FCSTD DOCUMENT  (FreeCAD 0.19R24267 +148 (Git))
Label: Idle Plate
License: All rights reserved
LicenseURL: http://en.wikipedia.org/wiki/All_rights_reserved
objects: Sketcher::SketchObject×2, Part::Part2DObjectPython×1, PartDesign::Body×1
note: 4 computed .brp shape members not serialized (recipe doc carries the construction recipe); baked Part::Feature solids carry a one-line shape summary decoded from their .brp

FEATURE [Sketcher::SketchObject] Sketch
  FullyConstrained = false
  MapMode = 5
  Support = -> [XY_Plane]
  sketch-geometry (27):
    g0: Circle CenterX=0 CenterY=0 CenterZ=0 NormalX=0 NormalY=0 NormalZ=1 AngleXU=0 Radius=15
    g1: Circle CenterX=0 CenterY=0 CenterZ=0 NormalX=0 NormalY=0 NormalZ=1 AngleXU=0 Radius=25
    g2: Circle CenterX=-30 CenterY=71.7924 CenterZ=0 NormalX=0 NormalY=0 NormalZ=1 AngleXU=0 Radius=24
    g3: Circle CenterX=-30 CenterY=71.7924 CenterZ=0 NormalX=0 NormalY=0 NormalZ=1 AngleXU=0 Radius=12
    g4: ArcOfCircle CenterX=-110 CenterY=0 CenterZ=0 NormalX=0 NormalY=0 NormalZ=1 AngleXU=0 Radius=25 StartAngle=1.5708 EndAngle=4.71239
    g5: ArcOfCircle CenterX=-75 CenterY=1.2e-15 CenterZ=0 NormalX=0 NormalY=0 NormalZ=1 AngleXU=0 Radius=25 StartAngle=4.71239 EndAngle=7.85398
    g6: LineSegment StartX=-110 StartY=-25 StartZ=0 EndX=-75 EndY=-25 EndZ=0
    g7: LineSegment StartX=-110 StartY=25 StartZ=0 EndX=-75 EndY=25 EndZ=0
    g8: ArcOfCircle CenterX=-110 CenterY=0 CenterZ=0 NormalX=0 NormalY=0 NormalZ=1 AngleXU=0 Radius=13 StartAngle=1.5708 EndAngle=4.71239
    g9: ArcOfCircle CenterX=-76.4586 CenterY=0 CenterZ=0 NormalX=0 NormalY=0 NormalZ=1 AngleXU=0 Radius=13 StartAngle=4.71239 EndAngle=7.85398
    g10: LineSegment StartX=-110 StartY=-13 StartZ=0 EndX=-76.4586 EndY=-13 EndZ=0
    g11: LineSegment StartX=-110 StartY=13 StartZ=0 EndX=-76.4586 EndY=13 EndZ=0
    g12: ArcOfCircle CenterX=79.9751 CenterY=0.000354198 CenterZ=0 NormalX=0 NormalY=0 NormalZ=1 AngleXU=0 Radius=12 StartAngle=3.04319 EndAngle=6.18992
    g13: ArcOfCircle CenterX=42.853 CenterY=65.8804 CenterZ=0 NormalX=0 NormalY=0 NormalZ=1 AngleXU=0 Radius=12 StartAngle=1.11953 EndAngle=4.26626
    g14: ArcOfCircle CenterX=42.853 CenterY=65.8804 CenterZ=0 NormalX=0 NormalY=0 NormalZ=1 AngleXU=0 Radius=23.9932 StartAngle=1.11953 EndAngle=4.28028
    g15: ArcOfCircle CenterX=-105.35 CenterY=76.497 CenterZ=0 NormalX=0 NormalY=0 NormalZ=1 AngleXU=0 Radius=51.497 StartAngle=4.71239 EndAngle=6.22083
    g16: ArcOfCircle CenterX=7.39019 CenterY=80.6675 CenterZ=0 NormalX=0 NormalY=0 NormalZ=1 AngleXU=0 Radius=14.4291 StartAngle=3.37464 EndAngle=5.88813
    g17: ArcOfCircle CenterX=13.9205 CenterY=6.17871 CenterZ=0 NormalX=0 NormalY=0 NormalZ=1 AngleXU=0 Radius=90.3361 StartAngle=6.18992 EndAngle=7.40272
    g18: ArcOfCircle CenterX=15.8002 CenterY=7.21933 CenterZ=0 NormalX=0 NormalY=0 NormalZ=1 AngleXU=0 Radius=40.6054 StartAngle=6.17117 EndAngle=7.42188
    g19: LineSegment StartX=-110 StartY=-25 StartZ=0 EndX=-16.1843 EndY=-43.4398 EndZ=0
    g20: LineSegment StartX=17.5699 StartY=-34.5542 StartZ=0 EndX=35.6596 EndY=-19.0405 EndZ=0
    g21: LineSegment StartX=53.6215 StartY=-15.8217 StartZ=0 EndX=70.8829 EndY=-22.206 EndZ=0
    g22: ArcOfCircle CenterX=-8.46974 CenterY=-4.19076 CenterZ=0 NormalX=0 NormalY=0 NormalZ=1 AngleXU=0 Radius=40 StartAngle=4.51831 EndAngle=5.42128
    g23: ArcOfCircle CenterX=47.3774 CenterY=-32.704 CenterZ=0 NormalX=0 NormalY=0 NormalZ=1 AngleXU=0 Radius=18 StartAngle=1.21654 EndAngle=2.27969
    g24: ArcOfCircle CenterX=13.9205 CenterY=6.17872 CenterZ=0 NormalX=0 NormalY=0 NormalZ=1 AngleXU=0 Radius=78.3429 StartAngle=6.18992 EndAngle=7.40272
    g25: ArcOfCircle CenterX=14.438 CenterY=6.47035 CenterZ=0 NormalX=0 NormalY=0 NormalZ=1 AngleXU=0 Radius=53.8556 StartAngle=6.18478 EndAngle=7.40786
    g26: ArcOfCircle CenterX=79.9845 CenterY=-0.000734032 CenterZ=0 NormalX=0 NormalY=0 NormalZ=1 AngleXU=0 Radius=23.9837 StartAngle=3.02957 EndAngle=6.18992
  constraints (52):
    c: Coincident(g0,g-1)
    c: Coincident(g1,g0)
    c: Coincident(g3,g2)
    c: Diameter(g3) = 24
    c: DistanceX(g2,g0) = 30
    c: Tangent(g4,g7) = 1.5708
    c: Tangent(g4,g6) = -1.5708
    c: Tangent(g6,g5) = -1.5708
    c: Tangent(g7,g5) = 1.5708
    c: Horizontal(g6)
    c: Equal(g4,g5)
    c: PointOnObject(g4,g-1)
    c: Tangent(g8,g11) = 1.5708
    c: Tangent(g8,g10) = -1.5708
    c: Tangent(g10,g9) = -1.5708
    c: Tangent(g11,g9) = 1.5708
    c: Horizontal(g10)
    c: Equal(g8,g9)
    c: Coincident(g8,g4)
    c: DistanceX(g4,g5) = 35
    c: Radius(g4) = 25
    c: Radius(g1) = 25
    c: Radius(g8) = 13
    c: Radius(g0) = 15
    c: Radius(g12) = 12
    c: Coincident(g13,g14)
    c: Equal(g12,g13) = 13
    c: PointOnObject(g15,g7)
    c: PointOnObject(g15,g2)
    c: Tangent(g2,g15)
    c: Tangent(g7,g15)
    c: PointOnObject(g16,g2)
    c: PointOnObject(g16,g14)
    c: Tangent(g2,g16)
    c: Tangent(g16,g14)
    c: Coincident(g19,g4)
    c: Tangent(g19,g22) = -1.5708
    c: Tangent(g20,g22) = -1.5708
    c: Tangent(g21,g23) = 1.5708
    c: Tangent(g20,g23) = 1.5708
    c: Tangent(g13,g24) = -1.5708
    c: Tangent(g13,g25) = 1.5708
    c: Tangent(g14,g18) = 1.5708
    c: Tangent(g14,g17) = -1.5708
    c: Tangent(g26,g18) = 1.5708
    c: Tangent(g12,g25) = 1.5708
    c: Tangent(g12,g24) = -1.5708
    c: Tangent(g21,g26)
    c: Radius(g2) = 24
    c: Tangent(g26,g17) = -1.5708
    c: Radius(g23) = 18
    c: Radius(g22) = 40
FEATURE [Part::Part2DObjectPython] Clone2D  label="Sketch (2D)"  # Draft 2D object (typed FeaturePython)
  Fuse = false
  Objects = -> [Sketch]
  Scale = (1,1,1)
FEATURE [Sketcher::SketchObject] Sketch001
  ExternalGeometry = -> [Sketch]
  FullyConstrained = false
  MapMode = 2
  Support = -> [Sketch]
  sketch-geometry (9):
    g0: ArcOfCircle CenterX=-105.554 CenterY=76.5097 CenterZ=0 NormalX=0 NormalY=0 NormalZ=1 AngleXU=0 Radius=51.7012 StartAngle=4.62629 EndAngle=6.22083
    g1: ArcOfCircle CenterX=-30 CenterY=71.7924 CenterZ=0 NormalX=0 NormalY=0 NormalZ=1 AngleXU=0 Radius=24 StartAngle=0.233051 EndAngle=3.07924
    g2: ArcOfCircle CenterX=7.39019 CenterY=80.6675 CenterZ=0 NormalX=0 NormalY=0 NormalZ=1 AngleXU=0 Radius=14.4291 StartAngle=3.37464 EndAngle=5.88813
    g3: ArcOfCircle CenterX=42.853 CenterY=65.8804 CenterZ=0 NormalX=0 NormalY=0 NormalZ=1 AngleXU=0 Radius=23.9932 StartAngle=1.11953 EndAngle=2.74654
    g4: ArcOfCircle CenterX=13.9205 CenterY=6.17871 CenterZ=0 NormalX=0 NormalY=0 NormalZ=1 AngleXU=0 Radius=90.3361 StartAngle=6.18992 EndAngle=7.40272
    g5: ArcOfCircle CenterX=80.8999 CenterY=0.000628356 CenterZ=0 NormalX=0 NormalY=0 NormalZ=1 AngleXU=0 Radius=23.0725 StartAngle=4.26329 EndAngle=6.18617
    g6: ArcOfCircle CenterX=-110 CenterY=1.6e-15 CenterZ=0 NormalX=0 NormalY=0 NormalZ=1 AngleXU=0 Radius=25 StartAngle=1.5708 EndAngle=4.71239
    g7: ArcOfCircle CenterX=95.5715 CenterY=97.5997 CenterZ=0 NormalX=0 NormalY=0 NormalZ=1 AngleXU=0 Radius=120.931 StartAngle=4.35813 EndAngle=4.50679
    g8: ArcOfCircle CenterX=47.3774 CenterY=-32.704 CenterZ=0 NormalX=0 NormalY=0 NormalZ=1 AngleXU=0 Radius=18 StartAngle=1.21654 EndAngle=2.27969
  constraints (20):
    c: Coincident(g0,g-12)
    c: Coincident(g1,g0)
    c: Coincident(g1,g-4)
    c: Coincident(g2,g1)
    c: Coincident(g2,g-4)
    c: Tangent(g2,g-4)
    c: Coincident(g3,g2)
    c: Coincident(g3,g-6)
    c: Tangent(g3,g-5)
    c: Coincident(g4,g3)
    c: Tangent(g4,g-6)
    c: Coincident(g6,g0)
    c: Coincident(g6,g-11)
    c: Tangent(g6,g-11)
    c: Coincident(g7,g5)
    c: Coincident(g7,g-15)
    c: Tangent(g7,g-15)
    c: Coincident(g8,g7)
    c: Coincident(g8,g-9)
    c: Tangent(g8,g-8)
FEATURE [PartDesign::Body] Body
  Group = -> [Sketch,Clone2D,Sketch001]
  Origin = -> Origin
